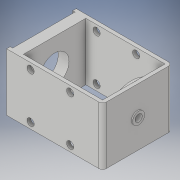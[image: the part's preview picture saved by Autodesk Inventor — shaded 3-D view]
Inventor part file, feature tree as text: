
AUTODESK INVENTOR PART (.ipt)
format: ipt  version: 2017 (Build 210142000, 142)  size: 221,184 bytes
history: native  units: in
note: dims shown in document units (in); Inventor stores cm internally (conversion verified against a paired STEP export)
features: extrude x10, sketch x10, fillet x2
ambient origin geometry x8: Origin, YZ Plane, XZ Plane, XY Plane, X Axis, Y Axis, Z Axis, Center Point
bodies: Solid1 (feature_tree)
feature tree (22):
  extrude  "Extrusion1"  Depth=0.9449in
  extrude  "Extrusion2"  Depth=0.0591in
  extrude  "Extrusion3"  Depth=0.9449in
  extrude  "Extrusion4"  Depth=0.1181in
  extrude  "Extrusion5"  Depth=0.0197in TaperAngle=0.0deg
  extrude  "Extrusion6"  Depth=0.0591in TaperAngle=0.0deg
  extrude  "Extrusion7"  Depth=0.9449in
  fillet  "Fillet1"  Radius=0.1772in
  fillet  "Fillet2"  Radius=0.9449in
  extrude  "Extrusion8"  Depth=0.4724in
  extrude  "Extrusion9"  Depth=0.0394in TaperAngle=0.0deg
  extrude  "Extrusion10"  Depth=0.0591in
  sketch  "Sketch1"  dims[d0=1.5748in d1=0.9449in]
  sketch  "Sketch2"  dims[d2=1.1417in d3=0.0in d4=0.0591in]
  sketch  "Sketch3"  dims[d5=0.0591in d6=0.9449in]
  sketch  "Sketch4"  dims[d7=1.5157in d8=0.0in d9=0.1181in]
  sketch  "Sketch5"  dims[d10=0.1969in d11=0.0197in d12=0.0in]
  sketch  "Sketch6"  dims[d13=0.1181in d14=0.0591in d15=0.0in]
  sketch  "Sketch7"  dims[d16=0.0394in d17=0.9449in d18=0.1772in d19=0.9449in]
  sketch  "Sketch8"  dims[d20=1.0236in d21=0.0in d22=0.4724in]
  sketch  "Sketch9"  dims[d23=0.1772in d24=0.0in d25=0.0394in d26=0.0in]
  sketch  "Sketch10"  dims[d27=0.0591in d28=0.0591in d29=0.3937in d30=0.9449in d31=0.3937in d32=0.8465in d33=0.8465in d34=0.1181in d35=0.1181in d36=1.1417in d37=0.0in d38=1.0433in d39=0.1181in d40=0.1181in d41=1.1417in d42=0.0in d43=0.1969in d44=0.0394in d45=0.0in]
